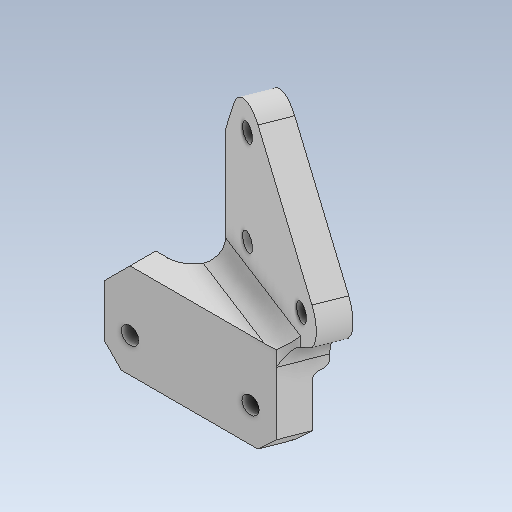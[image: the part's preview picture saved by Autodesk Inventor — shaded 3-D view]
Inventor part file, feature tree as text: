
AUTODESK INVENTOR PART (.ipt)
format: ipt  version: 2020 (Build 240168000, 168)  size: 186,368 bytes
history: native  units: mm
features: sketch x9, other x3
ambient origin geometry x8: Origin, YZ Plane, XZ Plane, XY Plane, X Axis, Y Axis, Z Axis, Center Point
bodies: Solid1 (feature_tree)
feature tree (12):
  other  "body_conn_1.ipt"
  other  "Solid1::body_conn_1.ipt"
  other  "TaggingFeature1"
  sketch  "Sketch1"  dims[d0=10.0mm]
  sketch  "Sketch2"
  sketch  "Sketch3"
  sketch  "Sketch4"
  sketch  "Sketch5"
  sketch  "Sketch6"
  sketch  "Sketch7"
  sketch  "Sketch8"
  sketch  "Sketch9"
